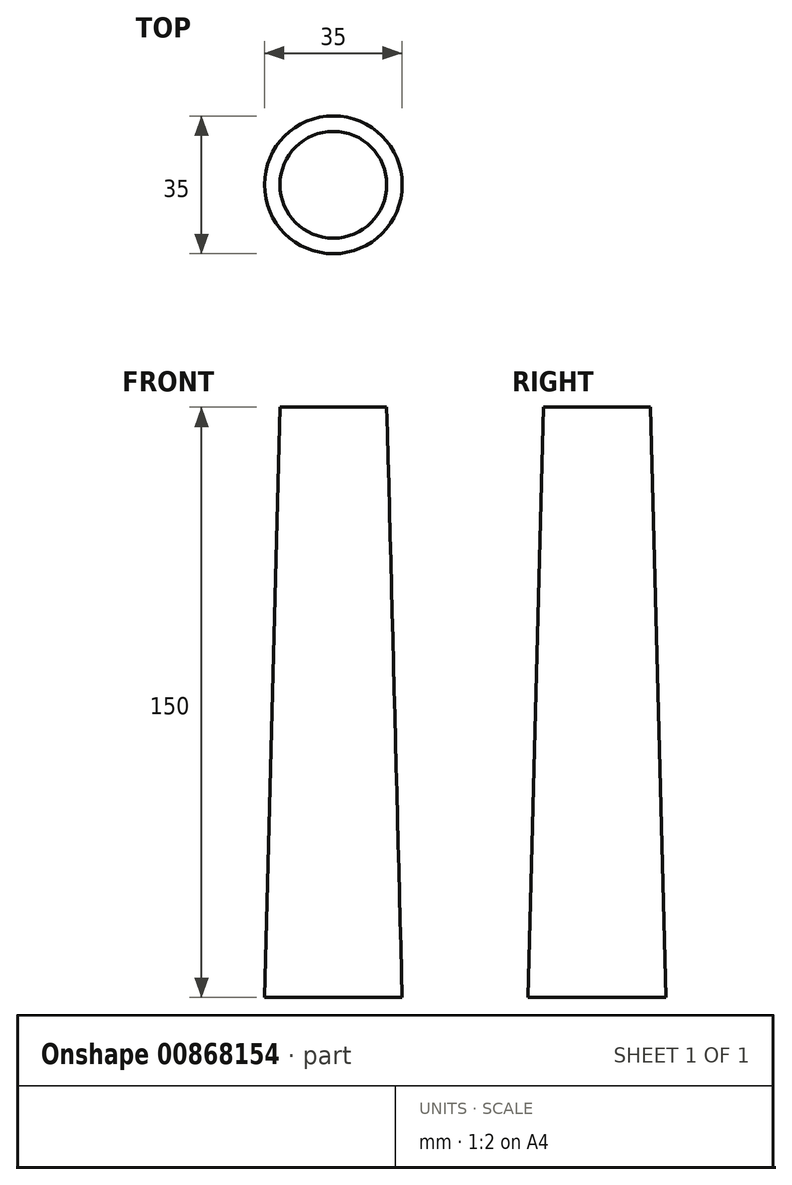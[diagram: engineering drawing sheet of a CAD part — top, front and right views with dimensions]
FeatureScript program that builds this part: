
annotation { "Feature Type Name" : "Feature", "Feature Type Description" : "" }
export const myFeature = defineFeature(function(context is Context, id is Id, definition is map)
    precondition{}
    {
        {
            var Q0;
            Q0=qCreatedBy(makeId("Top.planeOp"),FACE);
            var sketch = newSketch(context, id + "F0", { "sketchPlane" : qUnion([Q0])});
            skCircle(sketch, "E0", {"center": v(0, 0) * mm, "radius": 17.5 * mm});
            skSolve(sketch);
        }
        {
            var Q0;
            Q0=makeQuery(id+"F0.imprint","IMPRINT",FACE,{"disambiguationData":[TD([[makeQuery(id+"F0.imprint","IMPRINT",EDGE,{"derivedFrom":sQuery(id+"F0.wireOp",EDGE,"E0")}),1.0]])]});
            extrude(context, id + "F1", {"entities" : qUnion([Q0]), "depth" : 150 * mm, "offsetDistance" : 25 * mm, "hasDraft" : true, "draftAngle" : 1.5 * degree, "draftPullDirection" : true});
        }
    });
